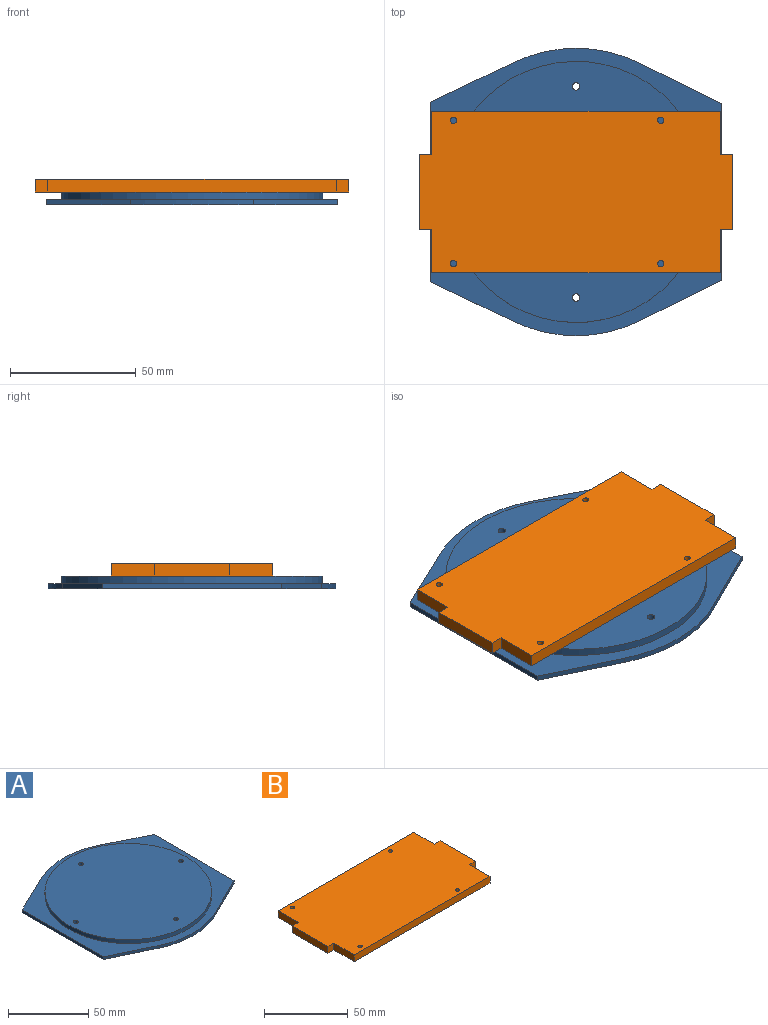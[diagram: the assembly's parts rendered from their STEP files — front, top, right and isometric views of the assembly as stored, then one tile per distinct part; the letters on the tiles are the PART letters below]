
ASSEMBLY  parts=2 mates=1
PART A: 16 faces, bbox 116x114.5x5 mm
  f0: plane 116x114.5mm, normal (0,0,-1), area 11252.1mm2, adj f2,f3,f4,f5,f7,f8,f9,f10
  f1: cylinder r=52mm len=104mm, axis (0,0,-1), area 980.2mm2, adj f6,f15
  f2: cylinder r=1.5mm len=5mm, axis (0,0,-1), area 47.1mm2, adj f0,f6
  f3: cylinder r=1.5mm len=5mm, axis (0,0,-1), area 47.1mm2, adj f0,f6
  f4: cylinder r=1.5mm len=5mm, axis (0,0,-1), area 47.1mm2, adj f0,f6
  f5: cylinder r=1.5mm len=5mm, axis (0,0,-1), area 47.1mm2, adj f0,f6
  f6: plane 104x104mm, normal (0,0,1), area 8466.6mm2, adj f1,f2,f3,f4,f5
  f7: cylinder r=57.25mm len=49.18mm, axis (0,0,-1), area 101.7mm2, adj f0,f8,f14,f15
  f8: plane 33.41x15.89mm, normal (-0.43,-0.9,0), area 74mm2, adj f0,f7,f9,f15
  f9: plane 71.62x2mm, normal (-1,0,0), area 143.2mm2, adj f0,f8,f10,f15
  f10: plane 33.41x15.89mm, normal (-0.43,0.9,0), area 74mm2, adj f0,f9,f11,f15
  f11: cylinder r=57.25mm len=49.18mm, axis (0,0,-1), area 101.7mm2, adj f0,f10,f12,f15
  f12: plane 33.41x16.48mm, normal (0.44,0.9,0), area 74.5mm2, adj f0,f11,f13,f15
  f13: plane 70.44x2mm, normal (1,0,0), area 140.9mm2, adj f0,f12,f14,f15
  f14: plane 33.41x16.48mm, normal (0.44,-0.9,0), area 74.5mm2, adj f0,f7,f13,f15
  f15: plane 116x114.5mm, normal (0,0,1), area 2785.5mm2, adj f1,f7,f8,f9,f10,f11,f12,f13
PART B: 18 faces, bbox 125x64.5x5 mm
  f0: plane 115x5mm, normal (0,-1,0), area 575mm2, adj f1,f11,f16,f17
  f1: plane 17.25x5mm, normal (1,0,0), area 86.3mm2, adj f0,f2,f16,f17
  f2: plane 5x5mm, normal (0,-1,0), area 25mm2, adj f1,f3,f16,f17
  f3: plane 30x5mm, normal (1,0,0), area 150mm2, adj f2,f4,f16,f17
  f4: plane 5x5mm, normal (0,1,0), area 25mm2, adj f3,f5,f16,f17
  f5: plane 17.25x5mm, normal (1,0,0), area 86.3mm2, adj f4,f6,f16,f17
  f6: plane 115x5mm, normal (0,1,0), area 575mm2, adj f5,f7,f16,f17
  f7: plane 17.25x5mm, normal (-1,0,0), area 86.3mm2, adj f6,f8,f16,f17
  f8: plane 5x4.98mm, normal (0,1,0), area 24.9mm2, adj f7,f9,f16,f17
  f9: plane 30x5mm, normal (-1,0,0), area 150mm2, adj f8,f10,f16,f17
  f10: plane 5x5mm, normal (0,-1,0), area 25mm2, adj f9,f11,f16,f17
  f11: plane 17.25x5mm, normal (-1,0,0), area 86.3mm2, adj f0,f10,f16,f17
  f12: cylinder r=1.25mm len=5mm, axis (0,0,-1), area 39.3mm2, adj f16,f17
  f13: cylinder r=1.25mm len=5mm, axis (0,0,-1), area 39.3mm2, adj f16,f17
  f14: cylinder r=1.25mm len=5mm, axis (0,0,-1), area 39.3mm2, adj f16,f17
  f15: cylinder r=1.25mm len=5mm, axis (0,0,-1), area 39.3mm2, adj f16,f17
  f16: plane 124.98x64.5mm, normal (0,0,1), area 7696.9mm2, adj f0,f1,f2,f3,f4,f5,f6,f7
  f17: plane 124.98x64.5mm, normal (0,0,-1), area 7696.9mm2, adj f0,f1,f2,f3,f4,f5,f6,f7
PLACE A t=(-31.34,6.44,31.58)mm
PLACE B t=(-31.37,6.44,36.58)mm
MATE fastened B.f17 <-> A.f1  axis (0,0,-1) through (-31.34,6.44,36.58)mm
